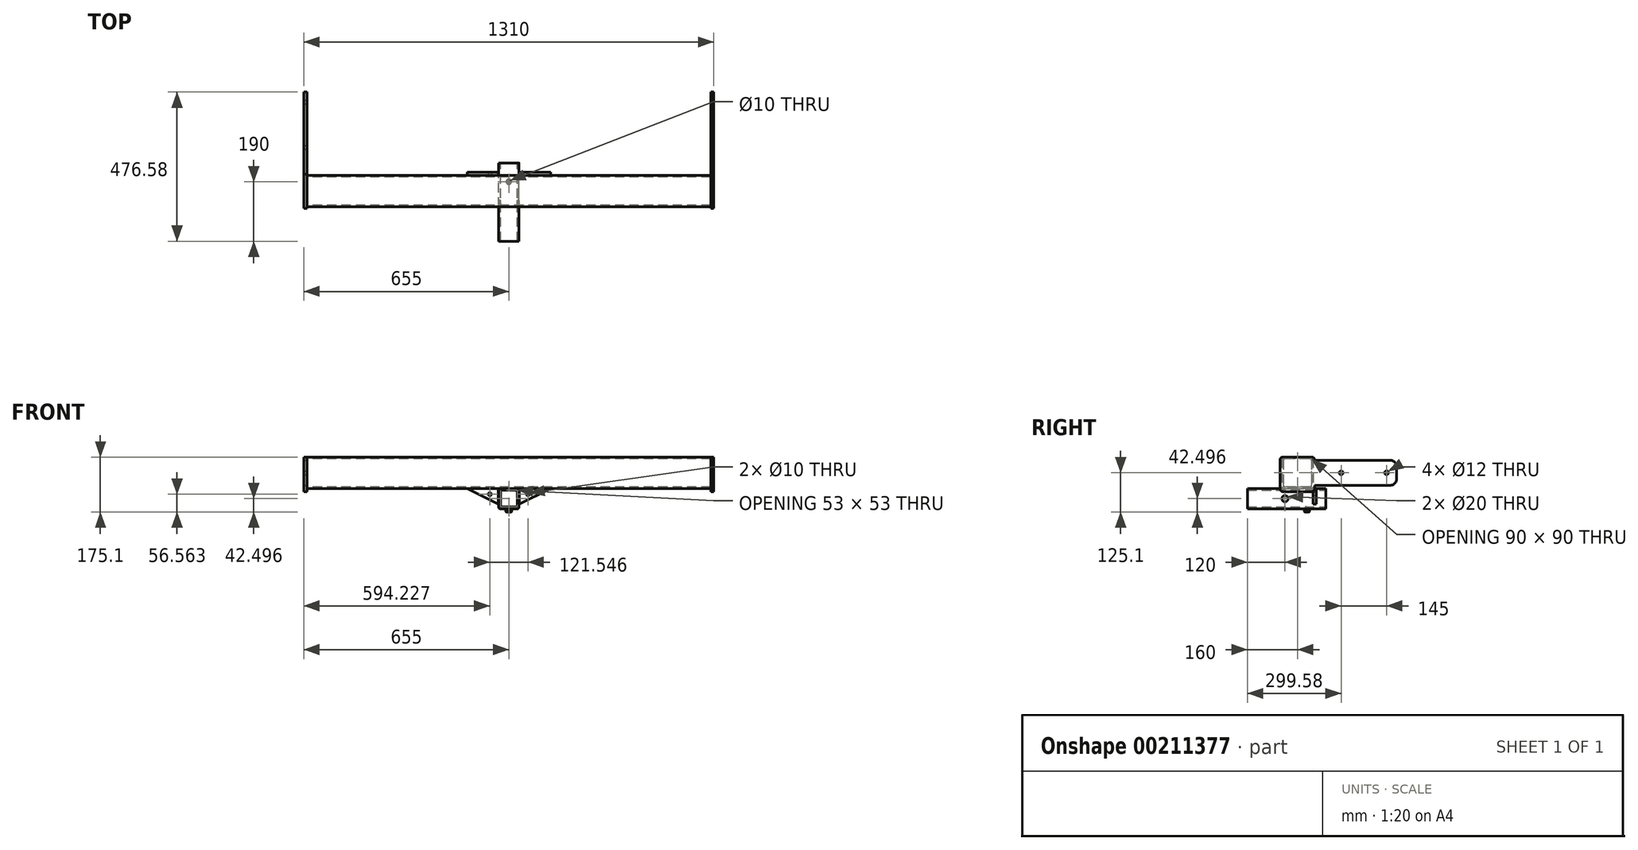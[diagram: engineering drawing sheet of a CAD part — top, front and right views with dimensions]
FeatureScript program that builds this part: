
annotation { "Feature Type Name" : "Feature", "Feature Type Description" : "" }
export const myFeature = defineFeature(function(context is Context, id is Id, definition is map)
    precondition{}
    {
        {
            var Q0;
            Q0=qCreatedBy(makeId("Right.planeOp"),FACE);
            var sketch = newSketch(context, id + "F0", { "sketchPlane" : qUnion([Q0])});
            skLineSegment(sketch, "E0.bottom", {"start": v(45.1, 50) * mm, "end": v(-45.1, 50) * mm});
            skLineSegment(sketch, "E0.top", {"start": v(45.1, -50) * mm, "end": v(-45.1, -50) * mm});
            skLineSegment(sketch, "E0.left", {"start": v(50, 45.1) * mm, "end": v(50, -45.1) * mm});
            skLineSegment(sketch, "E0.right", {"start": v(-50, 45.1) * mm, "end": v(-50, -45.1) * mm});
            skPoint(sketch, "E0.middle", {"position": v(0, 0) * mm});
            skLineSegment(sketch, "E1.bottom", {"start": v(40.1, 45) * mm, "end": v(-40.1, 45) * mm});
            skLineSegment(sketch, "E1.top", {"start": v(40.1, -45) * mm, "end": v(-40.1, -45) * mm});
            skLineSegment(sketch, "E1.left", {"start": v(45, 40.1) * mm, "end": v(45, -40.1) * mm});
            skLineSegment(sketch, "E1.right", {"start": v(-45, 40.1) * mm, "end": v(-45, -40.1) * mm});
            skPoint(sketch, "E2.visualSharp", {"position": v(50, 50) * mm});
            skArc(sketch, "E2.filletArc", {"start": v(50, 45.1) * mm, "mid": v(48.56, 48.56) * mm, "end": v(45.1, 50) * mm});
            skPoint(sketch, "E3.visualSharp", {"position": v(-50, 50) * mm});
            skArc(sketch, "E3.filletArc", {"start": v(-45.1, 50) * mm, "mid": v(-48.56, 48.56) * mm, "end": v(-50, 45.1) * mm});
            skPoint(sketch, "E4.visualSharp", {"position": v(-50, -50) * mm});
            skArc(sketch, "E4.filletArc", {"start": v(-50, -45.1) * mm, "mid": v(-48.56, -48.56) * mm, "end": v(-45.1, -50) * mm});
            skPoint(sketch, "E5.visualSharp", {"position": v(50, -50) * mm});
            skArc(sketch, "E5.filletArc", {"start": v(45.1, -50) * mm, "mid": v(48.56, -48.56) * mm, "end": v(50, -45.1) * mm});
            skPoint(sketch, "E6.visualSharp", {"position": v(-45, 45) * mm});
            skArc(sketch, "E6.filletArc", {"start": v(-40.1, 45) * mm, "mid": v(-43.56, 43.56) * mm, "end": v(-45, 40.1) * mm});
            skPoint(sketch, "E7.visualSharp", {"position": v(-45, -45) * mm});
            skArc(sketch, "E7.filletArc", {"start": v(-45, -40.1) * mm, "mid": v(-43.56, -43.56) * mm, "end": v(-40.1, -45) * mm});
            skPoint(sketch, "E8.visualSharp", {"position": v(45, -45) * mm});
            skArc(sketch, "E8.filletArc", {"start": v(40.1, -45) * mm, "mid": v(43.56, -43.56) * mm, "end": v(45, -40.1) * mm});
            skPoint(sketch, "E9.visualSharp", {"position": v(45, 45) * mm});
            skArc(sketch, "E9.filletArc", {"start": v(45, 40.1) * mm, "mid": v(43.56, 43.56) * mm, "end": v(40.1, 45) * mm});
            skSolve(sketch);
        }
        {
            var Q0;
            Q0=qSketchRegion(id+"F0",true);
            extrude(context, id + "F1", {"entities" : qUnion([Q0]), "depth" : 645 * mm, "hasSecondDirection" : true, "secondDirectionOppositeDirection" : true, "secondDirectionDepth" : 645 * mm});
        }
        {
            var Q0;
            Q0=makeQuery(id+"F1.opExtrude","CAP_FACE",FACE,{"disambiguationData":[OSD([sQuery(id+"F0.wireOp",EDGE,"E0.bottom"),sQuery(id+"F0.wireOp",EDGE,"E0.top"),sQuery(id+"F0.wireOp",EDGE,"E0.left"),sQuery(id+"F0.wireOp",EDGE,"E0.right"),sQuery(id+"F0.wireOp",EDGE,"E1.bottom"),sQuery(id+"F0.wireOp",EDGE,"E1.top"),sQuery(id+"F0.wireOp",EDGE,"E1.left"),sQuery(id+"F0.wireOp",EDGE,"E1.right"),sQuery(id+"F0.wireOp",EDGE,"E2.filletArc"),sQuery(id+"F0.wireOp",EDGE,"E3.filletArc"),sQuery(id+"F0.wireOp",EDGE,"E4.filletArc"),sQuery(id+"F0.wireOp",EDGE,"E5.filletArc"),sQuery(id+"F0.wireOp",EDGE,"E6.filletArc"),sQuery(id+"F0.wireOp",EDGE,"E7.filletArc"),sQuery(id+"F0.wireOp",EDGE,"E8.filletArc"),sQuery(id+"F0.wireOp",EDGE,"E9.filletArc")])],"isStart":true});
            var sketch = newSketch(context, id + "F2", { "sketchPlane" : qUnion([Q0])});
            skLineSegment(sketch, "E10", {"start": v(55.42, 50) * mm, "end": v(55.42, -60) * mm});
            skLineSegment(sketch, "E11", {"start": v(55.42, -60) * mm, "end": v(-54.58, -60) * mm});
            skLineSegment(sketch, "E12", {"start": v(-54.58, -60) * mm, "end": v(-54.58, -40) * mm});
            skLineSegment(sketch, "E13", {"start": v(-54.58, -40) * mm, "end": v(-296.58, -40) * mm});
            skLineSegment(sketch, "E14", {"start": v(-316.58, -20) * mm, "end": v(-316.58, 20) * mm});
            skLineSegment(sketch, "E15", {"start": v(-296.58, 40) * mm, "end": v(-54.58, 40) * mm});
            skLineSegment(sketch, "E16", {"start": v(55.42, 50) * mm, "end": v(-54.58, 50) * mm});
            skLineSegment(sketch, "E17", {"start": v(-54.58, 50) * mm, "end": v(-54.58, 40) * mm});
            skCircle(sketch, "E18", {"center": v(-139.58, 0) * mm, "radius": 6 * mm});
            skCircle(sketch, "E19", {"center": v(-284.58, 0) * mm, "radius": 6 * mm});
            skPoint(sketch, "E20.visualSharp", {"position": v(-316.58, 40) * mm});
            skArc(sketch, "E20.filletArc", {"start": v(-296.58, 40) * mm, "mid": v(-310.72, 34.14) * mm, "end": v(-316.58, 20) * mm});
            skPoint(sketch, "E21.visualSharp", {"position": v(-316.58, -40) * mm});
            skArc(sketch, "E21.filletArc", {"start": v(-316.58, -20) * mm, "mid": v(-310.72, -34.14) * mm, "end": v(-296.58, -40) * mm});
            skSolve(sketch);
        }
        {
            var Q0;
            Q0=qSketchRegion(id+"F2",true);
            extrude(context, id + "F3", {"entities" : qUnion([Q0]), "depth" : 10 * mm});
        }
        {
            var Q0;
            Q0=makeQuery(id+"F3.opExtrude","SWEPT_EDGE",EDGE,{"disambiguationData":[OSD([sQuery(id+"F2.wireOp",EDGE,"E16"),sQuery(id+"F2.wireOp",EDGE,"E17")])]});
            var Q1;
            Q1=makeQuery(id+"F3.opExtrude","SWEPT_EDGE",EDGE,{"disambiguationData":[OSD([sQuery(id+"F2.wireOp",EDGE,"E10"),sQuery(id+"F2.wireOp",EDGE,"E16")])]});
            var Q2;
            Q2=makeQuery(id+"F3.opExtrude","SWEPT_EDGE",EDGE,{"disambiguationData":[OSD([sQuery(id+"F2.wireOp",EDGE,"E10"),sQuery(id+"F2.wireOp",EDGE,"E11")])]});
            var Q3;
            Q3=makeQuery(id+"F3.opExtrude","SWEPT_EDGE",EDGE,{"disambiguationData":[OSD([sQuery(id+"F2.wireOp",EDGE,"E11"),sQuery(id+"F2.wireOp",EDGE,"E12")])]});
            fillet(context, id + "F4", {"entities" : qUnion([Q0, Q1, Q2, Q3]), "radius" : 8 * mm, "tangentPropagation" : true, "allowEdgeOverflow" : false});
        }
        {
            var Q0;
            Q0=makeQuery(id+"F3.opExtrude","SWEPT_BODY",BODY,{"disambiguationData":[OSD([sQuery(id+"F2.wireOp",EDGE,"E10"),sQuery(id+"F2.wireOp",EDGE,"E11"),sQuery(id+"F2.wireOp",EDGE,"E12"),sQuery(id+"F2.wireOp",EDGE,"E13"),sQuery(id+"F2.wireOp",EDGE,"E14"),sQuery(id+"F2.wireOp",EDGE,"E15"),sQuery(id+"F2.wireOp",EDGE,"E16"),sQuery(id+"F2.wireOp",EDGE,"E17"),sQuery(id+"F2.wireOp",EDGE,"E18"),sQuery(id+"F2.wireOp",EDGE,"E19"),sQuery(id+"F2.wireOp",EDGE,"E20.filletArc"),sQuery(id+"F2.wireOp",EDGE,"E21.filletArc")])]});
            var Q1;
            Q1=qCreatedBy(makeId("Right.planeOp"),FACE);
            mirror(context, id + "F5", {"entities" : qUnion([Q0]), "mirrorPlane" : qUnion([Q1])});
        }
        {
            var Q0;
            Q0=makeQuery(id+"F1.opExtrude","SWEPT_FACE",FACE,{"disambiguationData":[OSD([sQuery(id+"F0.wireOp",EDGE,"E0.right")])]});
            var sketch = newSketch(context, id + "F6", { "sketchPlane" : qUnion([Q0])});
            skLineSegment(sketch, "E22.bottom", {"start": v(-27.5, -50.1) * mm, "end": v(27.5, -50.1) * mm});
            skLineSegment(sketch, "E22.top", {"start": v(-27.5, -115.1) * mm, "end": v(27.5, -115.1) * mm});
            skLineSegment(sketch, "E22.left", {"start": v(-32.5, -55.1) * mm, "end": v(-32.5, -110.1) * mm});
            skLineSegment(sketch, "E22.right", {"start": v(32.5, -55.1) * mm, "end": v(32.5, -110.1) * mm});
            skPoint(sketch, "E22.middle", {"position": v(0, -82.6) * mm});
            skPoint(sketch, "E22.middle.positionSnap0", {"position": v(0, -45.1) * mm});
            skPoint(sketch, "E22.centerSnap0", {"position": v(0, -45.1) * mm});
            skLineSegment(sketch, "E23.bottom", {"start": v(-21.5, -56.1) * mm, "end": v(21.5, -56.1) * mm});
            skLineSegment(sketch, "E23.top", {"start": v(-21.5, -109.1) * mm, "end": v(21.5, -109.1) * mm});
            skLineSegment(sketch, "E23.left", {"start": v(-26.5, -61.1) * mm, "end": v(-26.5, -104.1) * mm});
            skLineSegment(sketch, "E23.right", {"start": v(26.5, -61.1) * mm, "end": v(26.5, -104.1) * mm});
            skPoint(sketch, "E24.visualSharp", {"position": v(-32.5, -115.1) * mm});
            skArc(sketch, "E24.filletArc", {"start": v(-32.5, -110.1) * mm, "mid": v(-31.04, -113.64) * mm, "end": v(-27.5, -115.1) * mm});
            skPoint(sketch, "E25.visualSharp", {"position": v(-32.5, -50.1) * mm});
            skArc(sketch, "E25.filletArc", {"start": v(-27.5, -50.1) * mm, "mid": v(-31.04, -51.57) * mm, "end": v(-32.5, -55.1) * mm});
            skPoint(sketch, "E26.visualSharp", {"position": v(32.5, -50.1) * mm});
            skArc(sketch, "E26.filletArc", {"start": v(32.5, -55.1) * mm, "mid": v(31.04, -51.57) * mm, "end": v(27.5, -50.1) * mm});
            skPoint(sketch, "E27.visualSharp", {"position": v(32.5, -115.1) * mm});
            skArc(sketch, "E27.filletArc", {"start": v(27.5, -115.1) * mm, "mid": v(31.04, -113.64) * mm, "end": v(32.5, -110.1) * mm});
            skPoint(sketch, "E28.visualSharp", {"position": v(26.5, -109.1) * mm});
            skArc(sketch, "E28.filletArc", {"start": v(21.5, -109.1) * mm, "mid": v(25.04, -107.64) * mm, "end": v(26.5, -104.1) * mm});
            skPoint(sketch, "E29.visualSharp", {"position": v(26.5, -56.1) * mm});
            skArc(sketch, "E29.filletArc", {"start": v(26.5, -61.1) * mm, "mid": v(25.04, -57.57) * mm, "end": v(21.5, -56.1) * mm});
            skPoint(sketch, "E30.visualSharp", {"position": v(-26.5, -56.1) * mm});
            skArc(sketch, "E30.filletArc", {"start": v(-21.5, -56.1) * mm, "mid": v(-25.04, -57.57) * mm, "end": v(-26.5, -61.1) * mm});
            skPoint(sketch, "E31.visualSharp", {"position": v(-26.5, -109.1) * mm});
            skArc(sketch, "E31.filletArc", {"start": v(-26.5, -104.1) * mm, "mid": v(-25.04, -107.64) * mm, "end": v(-21.5, -109.1) * mm});
            skSolve(sketch);
        }
        {
            var Q0;
            Q0=qSketchRegion(id+"F6",true);
            extrude(context, id + "F7", {"entities" : qUnion([Q0]), "depth" : 110 * mm, "hasSecondDirection" : true, "secondDirectionOppositeDirection" : true, "secondDirectionDepth" : 140 * mm});
        }
        {
            var Q0;
            Q0=makeQuery(id+"F7.opExtrude","SWEPT_FACE",FACE,{"disambiguationData":[OSD([sQuery(id+"F6.wireOp",EDGE,"E22.left")])]});
            var sketch = newSketch(context, id + "F8", { "sketchPlane" : qUnion([Q0])});
            skCircle(sketch, "E32", {"center": v(40, -82.6) * mm, "radius": 10 * mm});
            skSolve(sketch);
        }
        {
            var Q0;
            Q0=qSketchRegion(id+"F8",true);
            extrude(context, id + "F9", {"entities" : qUnion([Q0]), "operationType" : NewBodyOperationType.REMOVE, "oppositeDirection" : true, "depth" : 259 * mm});
        }
        {
            var Q0;
            Q0=makeQuery(id+"F7.opExtrude","SWEPT_FACE",FACE,{"disambiguationData":[OSD([sQuery(id+"F6.wireOp",EDGE,"E22.top")])]});
            var sketch = newSketch(context, id + "F10", { "sketchPlane" : qUnion([Q0])});
            skCircle(sketch, "E33.cCircle", {"center": v(0, -30) * mm, "radius": 8.11 * mm, "construction": true});
            skLineSegment(sketch, "E33.0", {"start": v(-9.37, -29.92) * mm, "end": v(-4.62, -21.85) * mm});
            skLineSegment(sketch, "E33.1", {"start": v(-4.62, -21.85) * mm, "end": v(4.75, -21.93) * mm});
            skLineSegment(sketch, "E33.2", {"start": v(4.75, -21.93) * mm, "end": v(9.37, -30.08) * mm});
            skLineSegment(sketch, "E33.3", {"start": v(9.37, -30.08) * mm, "end": v(4.62, -38.15) * mm});
            skLineSegment(sketch, "E33.4", {"start": v(4.62, -38.15) * mm, "end": v(-4.75, -38.07) * mm});
            skLineSegment(sketch, "E33.5", {"start": v(-4.75, -38.07) * mm, "end": v(-9.37, -29.92) * mm});
            skPoint(sketch, "E33.0.midPoint", {"position": v(-7, -25.89) * mm});
            skSolve(sketch);
        }
        {
            var Q0;
            Q0=qSketchRegion(id+"F10",true);
            extrude(context, id + "F11", {"entities" : qUnion([Q0]), "operationType" : NewBodyOperationType.ADD, "depth" : 10 * mm});
        }
        {
            var Q0;
            Q0=makeQuery(id+"F7.opExtrude","SWEPT_FACE",FACE,{"disambiguationData":[OSD([sQuery(id+"F6.wireOp",EDGE,"E22.top")])]});
            var sketch = newSketch(context, id + "F12", { "sketchPlane" : qUnion([Q0])});
            skCircle(sketch, "E34", {"center": v(0, -30) * mm, "radius": 5 * mm});
            skSolve(sketch);
        }
        {
            var Q0;
            Q0=qSketchRegion(id+"F12",true);
            extrude(context, id + "F13", {"entities" : qUnion([Q0]), "operationType" : NewBodyOperationType.REMOVE, "oppositeDirection" : true, "depth" : 25 * mm, "hasSecondDirection" : true, "secondDirectionOppositeDirection" : false, "secondDirectionDepth" : 25.8 * mm});
        }
        {
            var Q0;
            Q0=makeQuery(id+"F11.opExtrude","CAP_FACE",FACE,{"disambiguationData":[OSD([sQuery(id+"F10.wireOp",EDGE,"E33.0"),sQuery(id+"F10.wireOp",EDGE,"E33.1"),sQuery(id+"F10.wireOp",EDGE,"E33.2"),sQuery(id+"F10.wireOp",EDGE,"E33.3"),sQuery(id+"F10.wireOp",EDGE,"E33.4"),sQuery(id+"F10.wireOp",EDGE,"E33.5")])],"isStart":false});
            chamfer(context, id + "F14", {"entities" : qUnion([Q0]), "width" : 1 * mm, "tangentPropagation" : true});
        }
        {
            var Q0;
            Q0=makeQuery(id+"F1.opExtrude","SWEPT_FACE",FACE,{"disambiguationData":[OSD([sQuery(id+"F0.wireOp",EDGE,"E0.left")])]});
            var sketch = newSketch(context, id + "F15", { "sketchPlane" : qUnion([Q0])});
            skLineSegment(sketch, "E35", {"start": v(-33.28, -50.4) * mm, "end": v(-133.28, -50.4) * mm});
            skLineSegment(sketch, "E36", {"start": v(-133.28, -50.4) * mm, "end": v(-33.28, -100.4) * mm});
            skLineSegment(sketch, "E37", {"start": v(-33.28, -100.4) * mm, "end": v(-33.28, -50.4) * mm});
            skCircle(sketch, "E38", {"center": v(-60.77, -68.54) * mm, "radius": 5 * mm});
            skSolve(sketch);
        }
        {
            var Q0;
            Q0=qSketchRegion(id+"F15",true);
            extrude(context, id + "F16", {"entities" : qUnion([Q0]), "depth" : 10 * mm});
        }
        {
            var Q0;
            Q0=makeQuery(id+"F16.opExtrude","SWEPT_BODY",BODY,{"disambiguationData":[OSD([sQuery(id+"F15.wireOp",EDGE,"E35"),sQuery(id+"F15.wireOp",EDGE,"E36"),sQuery(id+"F15.wireOp",EDGE,"E37"),sQuery(id+"F15.wireOp",EDGE,"E38")])]});
            var Q1;
            Q1=qCreatedBy(makeId("Right.planeOp"),FACE);
            mirror(context, id + "F17", {"entities" : qUnion([Q0]), "mirrorPlane" : qUnion([Q1])});
        }
    });
